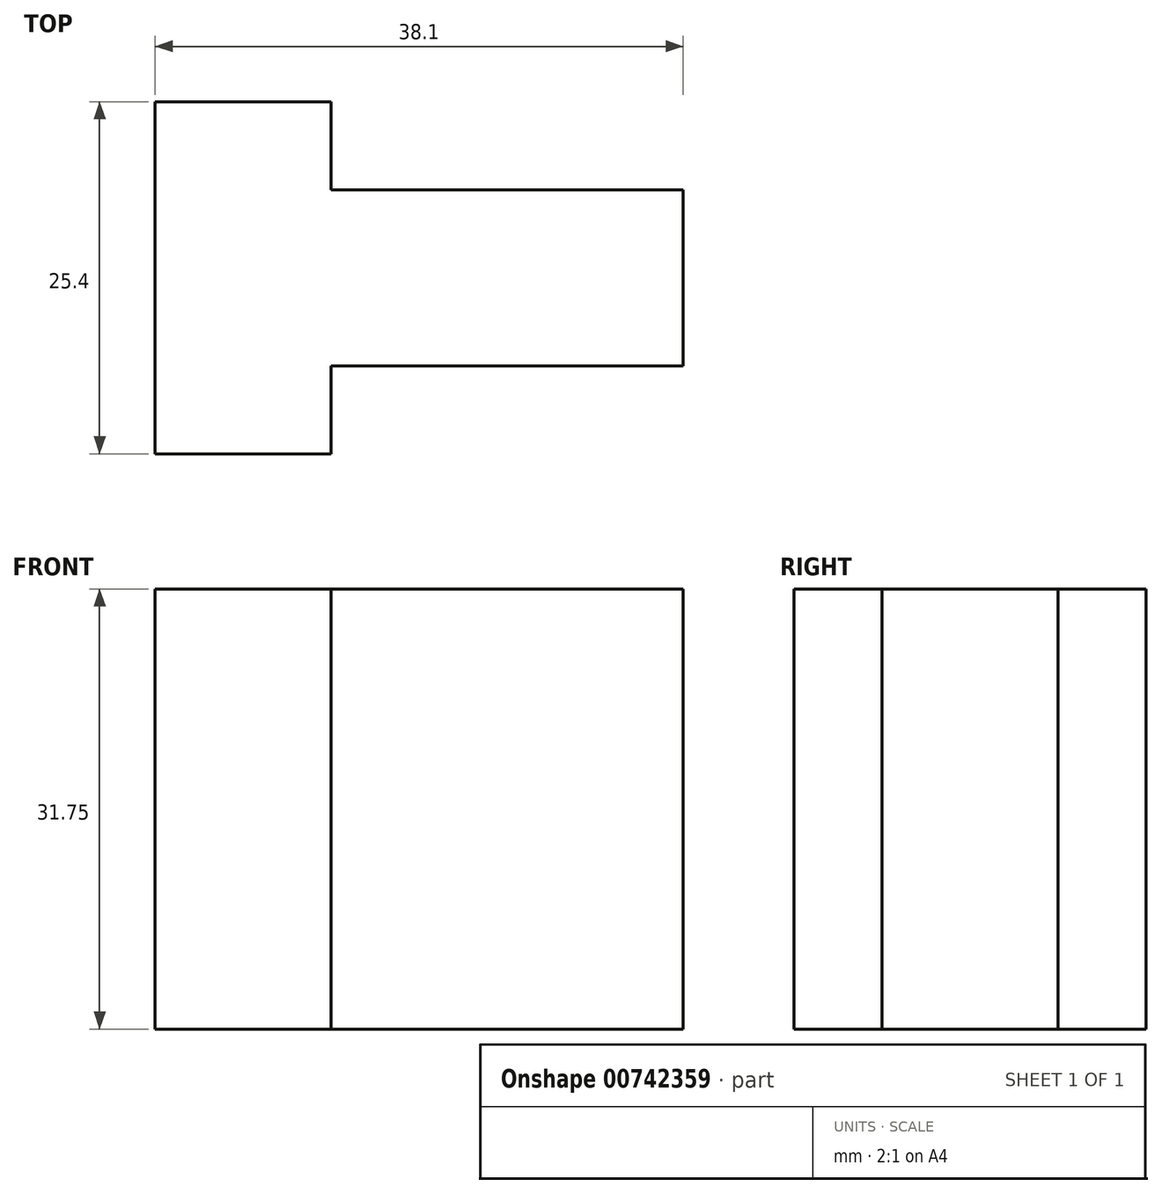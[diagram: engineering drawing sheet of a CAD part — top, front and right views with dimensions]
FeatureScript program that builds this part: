
annotation { "Feature Type Name" : "Feature", "Feature Type Description" : "" }
export const myFeature = defineFeature(function(context is Context, id is Id, definition is map)
    precondition{}
    {
        {
            var Q0;
            Q0=qCreatedBy(makeId("Front.planeOp"),FACE);
            var sketch = newSketch(context, id + "F0", { "sketchPlane" : qUnion([Q0])});
            skLineSegment(sketch, "E0", {"start": v(0, 31.75) * mm, "end": v(0, 0) * mm});
            skLineSegment(sketch, "E1", {"start": v(0, 0) * mm, "end": v(38.1, 0) * mm});
            skLineSegment(sketch, "E2", {"start": v(38.1, 0) * mm, "end": v(38.1, 31.75) * mm});
            skLineSegment(sketch, "E3", {"start": v(38.1, 31.75) * mm, "end": v(0, 31.75) * mm});
            skSolve(sketch);
        }
        {
            var Q0;
            Q0 = qSketchRegion(id + "F0", true);
            extrude(context, id + "F1", {"entities" : qUnion([Q0]), "depth" : 25.4 * mm, "offsetDistance" : 25.4 * mm});
        }
        {
            var Q0;
            Q0=makeQuery(id+"F1.opExtrude","CAP_FACE",FACE,{"disambiguationData":[OSD([sQuery(id+"F0.wireOp",EDGE,"E0"),sQuery(id+"F0.wireOp",EDGE,"E1"),sQuery(id+"F0.wireOp",EDGE,"E2"),sQuery(id+"F0.wireOp",EDGE,"E3")])],"isStart":false});
            var sketch = newSketch(context, id + "F2", { "sketchPlane" : qUnion([Q0])});
            skLineSegment(sketch, "E4", {"start": v(12.7, 0) * mm, "end": v(12.7, 31.75) * mm});
            skLineSegment(sketch, "E5", {"start": v(12.7, 31.75) * mm, "end": v(38.1, 31.75) * mm});
            skLineSegment(sketch, "E6", {"start": v(38.1, 31.75) * mm, "end": v(38.1, 0) * mm});
            skLineSegment(sketch, "E7", {"start": v(38.1, 0) * mm, "end": v(12.7, 0) * mm});
            skSolve(sketch);
        }
        {
            var Q0;
            Q0 = qSketchRegion(id + "F2", true);
            extrude(context, id + "F3", {"entities" : qUnion([Q0]), "operationType" : NewBodyOperationType.REMOVE, "oppositeDirection" : true, "depth" : 6.35 * mm, "offsetDistance" : 25.4 * mm});
        }
        {
            var Q0;
            Q0=makeQuery(id+"F1.opExtrude","CAP_FACE",FACE,{"disambiguationData":[OSD([sQuery(id+"F0.wireOp",EDGE,"E0"),sQuery(id+"F0.wireOp",EDGE,"E1"),sQuery(id+"F0.wireOp",EDGE,"E2"),sQuery(id+"F0.wireOp",EDGE,"E3")])],"isStart":true});
            var sketch = newSketch(context, id + "F4", { "sketchPlane" : qUnion([Q0])});
            skLineSegment(sketch, "E8", {"start": v(-12.7, 0) * mm, "end": v(-12.7, 31.75) * mm});
            skLineSegment(sketch, "E9", {"start": v(-12.7, 31.75) * mm, "end": v(-38.1, 31.75) * mm});
            skLineSegment(sketch, "E10", {"start": v(-38.1, 31.75) * mm, "end": v(-38.1, 0) * mm});
            skLineSegment(sketch, "E11", {"start": v(-38.1, 0) * mm, "end": v(-12.7, 0) * mm});
            skSolve(sketch);
        }
        {
            var Q0;
            Q0=makeQuery(id+"F4.imprint","IMPRINT",FACE,{"disambiguationData":[TD([[makeQuery(id+"F4.imprint","IMPRINT",EDGE,{"derivedFrom":sQuery(id+"F4.wireOp",EDGE,"E8")}),1.0]])]});
            extrude(context, id + "F5", {"entities" : qUnion([Q0]), "operationType" : NewBodyOperationType.REMOVE, "oppositeDirection" : true, "depth" : 6.35 * mm, "offsetDistance" : 25.4 * mm});
        }
    });
